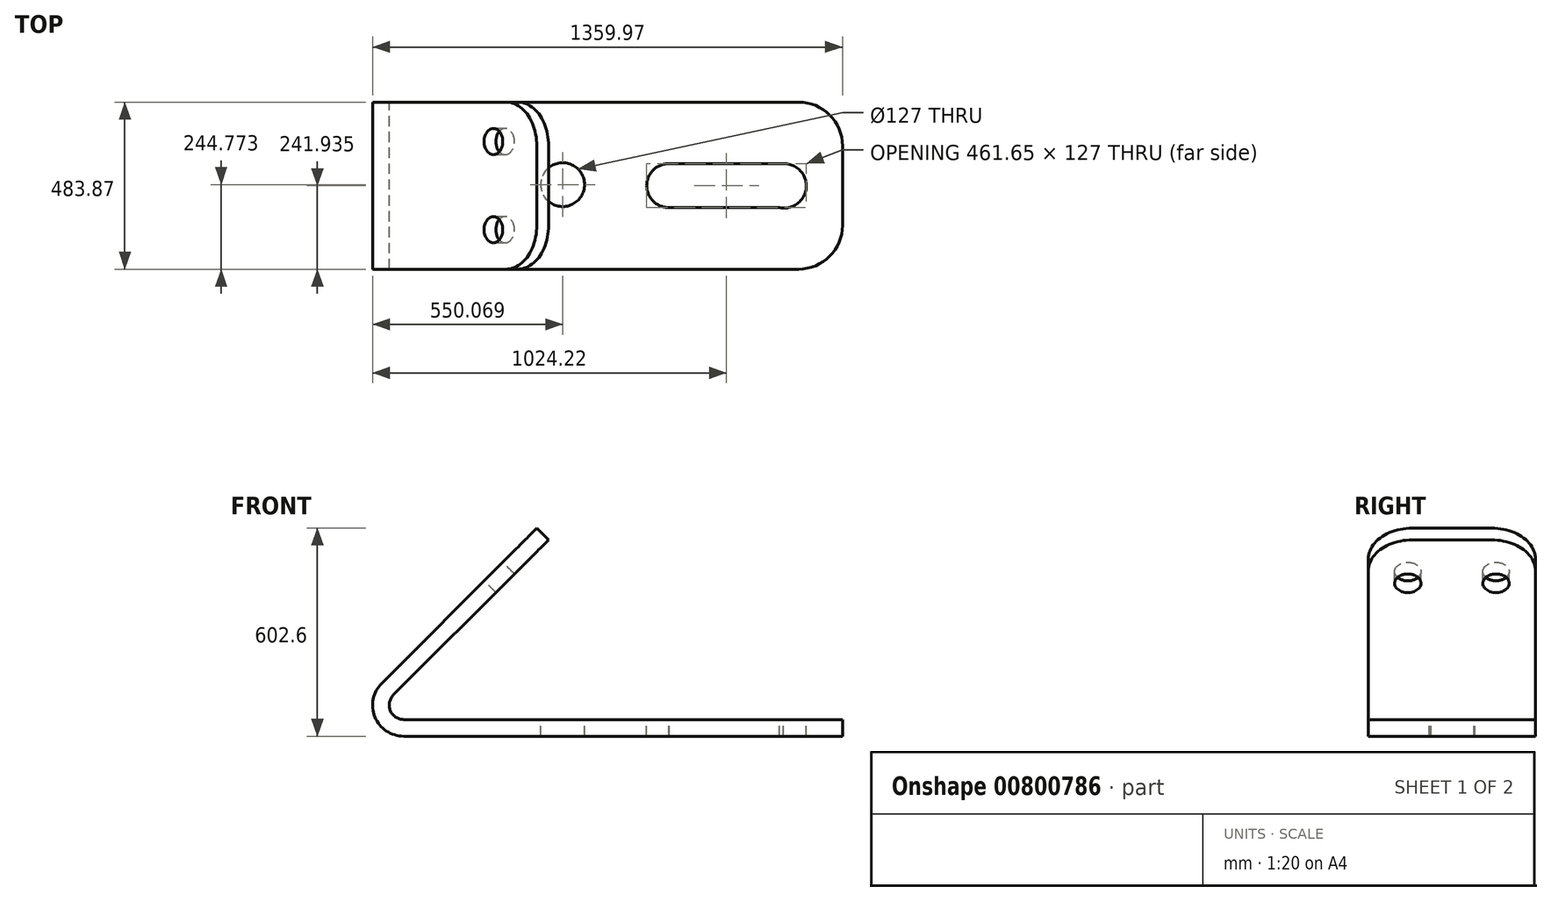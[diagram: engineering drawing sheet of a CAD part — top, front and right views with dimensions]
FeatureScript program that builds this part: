
annotation { "Feature Type Name" : "Feature", "Feature Type Description" : "" }
export const myFeature = defineFeature(function(context is Context, id is Id, definition is map)
    precondition{}
    {
        {
            var Q0;
            Q0=qCreatedBy(makeId("Front.planeOp"),FACE);
            var sketch = newSketch(context, id + "F0", { "sketchPlane" : qUnion([Q0])});
            skCircle(sketch, "E0", {"center": v(0, 0) * mm, "radius": 41.71 * mm});
            skCircle(sketch, "E1", {"center": v(0, 0) * mm, "radius": 89.97 * mm});
            skLineSegment(sketch, "E2", {"start": v(0, -89.97) * mm, "end": v(1270, -89.97) * mm});
            skLineSegment(sketch, "E3", {"start": v(-63.62, 63.62) * mm, "end": v(385.4, 512.63) * mm});
            skLineSegment(sketch, "E4", {"start": v(0, -41.71) * mm, "end": v(1270, -41.71) * mm});
            skLineSegment(sketch, "E5", {"start": v(-29.5, 29.5) * mm, "end": v(92.68, 151.67) * mm});
            skLineSegment(sketch, "E6", {"start": v(1270, -41.71) * mm, "end": v(1270, -89.97) * mm});
            skLineSegment(sketch, "E7", {"start": v(385.4, 512.63) * mm, "end": v(419.52, 478.5) * mm});
            skLineSegment(sketch, "E8", {"start": v(92.68, 151.67) * mm, "end": v(419.52, 478.5) * mm});
            skSolve(sketch);
        }
        {
            var Q0;
            {var subQ0=sQuery(id+"F0.wireOp",EDGE,"E2");Q0=makeQuery(id+"F0.imprint","IMPRINT",FACE,{"disambiguationData":[TD([[makeQuery(id+"F0.imprint","IMPRINT",EDGE,{"derivedFrom":subQ0}),1.0]])]});}
            var Q1;
            {var subQ0=sQuery(id+"F0.wireOp",EDGE,"E3");Q1=makeQuery(id+"F0.imprint","IMPRINT",FACE,{"disambiguationData":[TD([[makeQuery(id+"F0.imprint","IMPRINT",EDGE,{"derivedFrom":subQ0}),-1.0]])]});}
            var Q2;
            {var subQ2=sQuery(id+"F0.wireOp",EDGE,"E4");var subQ7=sQuery(id+"F0.wireOp",EDGE,"E0");var subQ8=makeQuery(id+"F0.imprint","INTERSECT",VERTEX,{"derivedFrom":[subQ7,subQ2]});Q2=makeQuery(id+"F0.imprint","IMPRINT",FACE,{"disambiguationData":[TD([[makeQuery(id+"F0.imprint","IMPRINT",EDGE,{"disambiguationData":[TD([[subQ8,1.0]])],"derivedFrom":subQ7}),-1.0]])]});}
            extrude(context, id + "F1", {"entities" : qUnion([Q0, Q1, Q2]), "depth" : 483.87 * mm, "offsetDistance" : 25.4 * mm});
        }
        {
            var Q0;
            Q0=makeQuery(id+"F1.opExtrude","CAP_EDGE",EDGE,{"disambiguationData":[OSD([sQuery(id+"F0.wireOp",EDGE,"E6")])],"isStart":false});
            var Q1;
            Q1=makeQuery(id+"F1.opExtrude","CAP_EDGE",EDGE,{"disambiguationData":[OSD([sQuery(id+"F0.wireOp",EDGE,"E6")])],"isStart":true});
            fillet(context, id + "F2", {"entities" : qUnion([Q0, Q1]), "radius" : 127 * mm, "tangentPropagation" : true, "allowEdgeOverflow" : false});
        }
        {
            var Q0;
            Q0=makeQuery(id+"F1.opExtrude","CAP_EDGE",EDGE,{"disambiguationData":[OSD([sQuery(id+"F0.wireOp",EDGE,"E7")])],"isStart":false});
            var Q1;
            Q1=makeQuery(id+"F1.opExtrude","CAP_EDGE",EDGE,{"disambiguationData":[OSD([sQuery(id+"F0.wireOp",EDGE,"E7")])],"isStart":true});
            fillet(context, id + "F3", {"entities" : qUnion([Q0, Q1]), "radius" : 127 * mm, "tangentPropagation" : true, "allowEdgeOverflow" : false});
        }
        {
            var Q0;
            Q0=qCreatedBy(makeId("Top.planeOp"),FACE);
            var sketch = newSketch(context, id + "F4", { "sketchPlane" : qUnion([Q0])});
            skLineSegment(sketch, "E9.bottom", {"start": v(765.7, -178.44) * mm, "end": v(1102.84, -178.44) * mm});
            skLineSegment(sketch, "E9.top", {"start": v(765.18, -305.44) * mm, "end": v(1114.47, -305.44) * mm});
            skLineSegment(sketch, "E9.left", {"start": v(703.42, -241.94) * mm, "end": v(703.42, -241.95) * mm});
            skLineSegment(sketch, "E9.right", {"start": v(1165.34, -241.94) * mm, "end": v(1165.34, -243.31) * mm});
            skArc(sketch, "E10", {"start": v(768.2, -178.44) * mm, "mid": v(703.42, -242.2) * mm, "end": v(768.7, -305.44) * mm});
            skPoint(sketch, "E10.first.point", {"position": v(703.42, -241.94) * mm});
            skPoint(sketch, "E10.second.point", {"position": v(768.2, -178.44) * mm});
            skPoint(sketch, "E10.third.point", {"position": v(768.7, -305.44) * mm});
            skArc(sketch, "E11", {"start": v(1087.78, -305.44) * mm, "mid": v(1165.07, -248.48) * mm, "end": v(1099.42, -178.44) * mm});
            skPoint(sketch, "E11.first.point", {"position": v(1087.78, -305.44) * mm});
            skPoint(sketch, "E11.second.point", {"position": v(1165.34, -241.94) * mm});
            skPoint(sketch, "E11.third.point", {"position": v(1099.42, -178.44) * mm});
            skPoint(sketch, "E12.orphan", {"position": v(703.42, -178.44) * mm});
            skPoint(sketch, "E13.orphan", {"position": v(703.42, -305.44) * mm});
            skPoint(sketch, "E14.orphan", {"position": v(1165.34, -305.44) * mm});
            skPoint(sketch, "E15.orphan", {"position": v(1165.34, -178.44) * mm});
            skCircle(sketch, "E16", {"center": v(460.1, -239.1) * mm, "radius": 63.5 * mm});
            skLineSegment(sketch, "E17", {"start": v(460.1, -239.1) * mm, "end": v(460.1, 171.57) * mm});
            skLineSegment(sketch, "E18", {"start": v(460.1, 171.57) * mm, "end": v(1272.9, 171.57) * mm});
            skLineSegment(sketch, "E19", {"start": v(1272.9, -162.28) * mm, "end": v(1272.9, 171.57) * mm});
            skSolve(sketch);
        }
        {
            var Q0;
            Q0 = qSketchRegion(id + "F4", true);
            extrude(context, id + "F5", {"entities" : qUnion([Q0]), "operationType" : NewBodyOperationType.REMOVE, "oppositeDirection" : true, "depth" : 262.9 * mm, "offsetDistance" : 25.4 * mm});
        }
        {
            var Q0;
            Q0=makeQuery(id+"F1.opExtrude","SWEPT_FACE",FACE,{"disambiguationData":[OSD([sQuery(id+"F0.wireOp",EDGE,"E3")])]});
            var sketch = newSketch(context, id + "F6", { "sketchPlane" : qUnion([Q0])});
            skCircle(sketch, "E20", {"center": v(114.3, 457.28) * mm, "radius": 38.1 * mm});
            skCircle(sketch, "E21", {"center": v(369.57, 457.2) * mm, "radius": 38.1 * mm});
            skSolve(sketch);
        }
        {
            var Q0;
            Q0=makeQuery(id+"F6.imprint","IMPRINT",FACE,{"disambiguationData":[TD([[makeQuery(id+"F6.imprint","IMPRINT",EDGE,{"derivedFrom":sQuery(id+"F6.wireOp",EDGE,"E20")}),1.0]])]});
            var Q1;
            Q1=makeQuery(id+"F6.imprint","IMPRINT",FACE,{"disambiguationData":[TD([[makeQuery(id+"F6.imprint","IMPRINT",EDGE,{"derivedFrom":sQuery(id+"F6.wireOp",EDGE,"E20")}),1.0]])]});
            var Q2;
            Q2=makeQuery(id+"F6.imprint","IMPRINT",FACE,{"disambiguationData":[TD([[makeQuery(id+"F6.imprint","IMPRINT",EDGE,{"derivedFrom":sQuery(id+"F6.wireOp",EDGE,"E21")}),1.0]])]});
            extrude(context, id + "F7", {"entities" : qUnion([Q0, Q1, Q2]), "operationType" : NewBodyOperationType.REMOVE, "oppositeDirection" : true, "depth" : 111.52 * mm, "offsetDistance" : 25.4 * mm});
        }
    });
